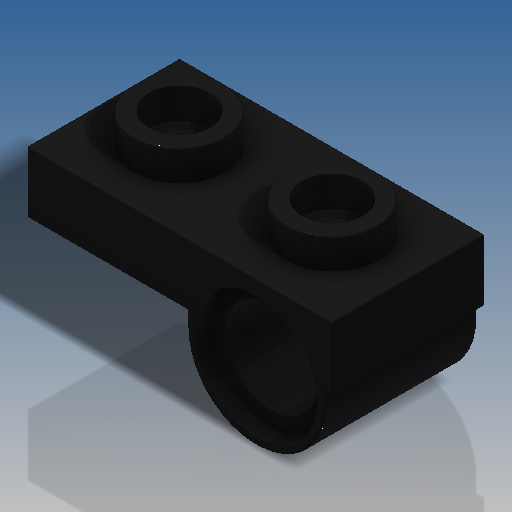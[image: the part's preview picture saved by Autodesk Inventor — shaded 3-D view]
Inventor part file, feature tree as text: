
AUTODESK INVENTOR PART (.ipt)
format: ipt  version: 2019.4 (Build 234330000, 330)  size: 1,702,912 bytes
history: native  units: in
note: dims shown in document units (in); Inventor stores cm internally (conversion verified against a paired STEP export)
features: extrude x6, sketch x5, other x2, fillet x1
ambient origin geometry x8: Origin, YZ Plane, XZ Plane, XY Plane, X Axis, Y Axis, Z Axis, Center Point
bodies: Solid1 (feature_tree)
feature tree (14):
  sketch  "Sketch2"  dims[d0=0.315in d1=0.6299in]
  extrude  "Extrusion1"  Depth=0.6299in
  extrude  "Extrusion2"  TaperAngle=0.0deg  [1 undecoded]
  extrude  "Extrusion3"  Depth=0.063in
  other  "LEGO_SM:1"
  other  "LEGO_SM:2"
  sketch  "Sketch4"  dims[d4=0.3307in d5=0.063in]
  extrude  "Extrusion4"  Depth=0.063in
  extrude  "Extrusion5"  TaperAngle=0.0deg  [1 undecoded]
  extrude  "Extrusion6"  Depth=0.0039in
  fillet  "Fillet1"  Radius=0.126in
  sketch  "Sketch3"  dims[d2=0.126in d3=0.0in]
  sketch  "Sketch5"  dims[d7=0.063in d8=0.063in]
  sketch  "Sketch6"  dims[d9=0.063in d10=0.0in d11=0.189in d12=0.126in d13=0.315in d14=0.063in d15=0.0in d16=0.1575in d17=0.1575in d18=0.189in d19=0.252in d20=0.2835in d21=0.315in d22=0.0in d23=0.315in d24=0.0in d25=0.252in d26=0.0in d27=0.0039in d28=0.0in d29=0.0in d30=0.0in d31=0.0in d32=0.0in d33=0.0in d34=0.0in d35=0.0in d36=0.0in d37=0.0055in d38=0.0513in d39=0.0197in d40=0.0245in d41=0.0055in d42=0.0097in d43=0.0197in d44=0.0245in d45=0.0197in d46=0.0111in d47=0.0124in d48=0.0245in d49=0.5428in d50=0.0055in d51=0.0513in d52=0.0197in d53=0.0245in d54=0.0055in d55=0.0097in d56=0.0197in d57=0.0245in d58=0.0197in d59=0.0111in d60=0.0124in d61=0.0245in d62=0.5428in]
note: 2 required parameter values undecoded (feature->parameter linkage not recoverable at this tier; creation-order binding heuristic only, values carry confidence <= 0.55)
